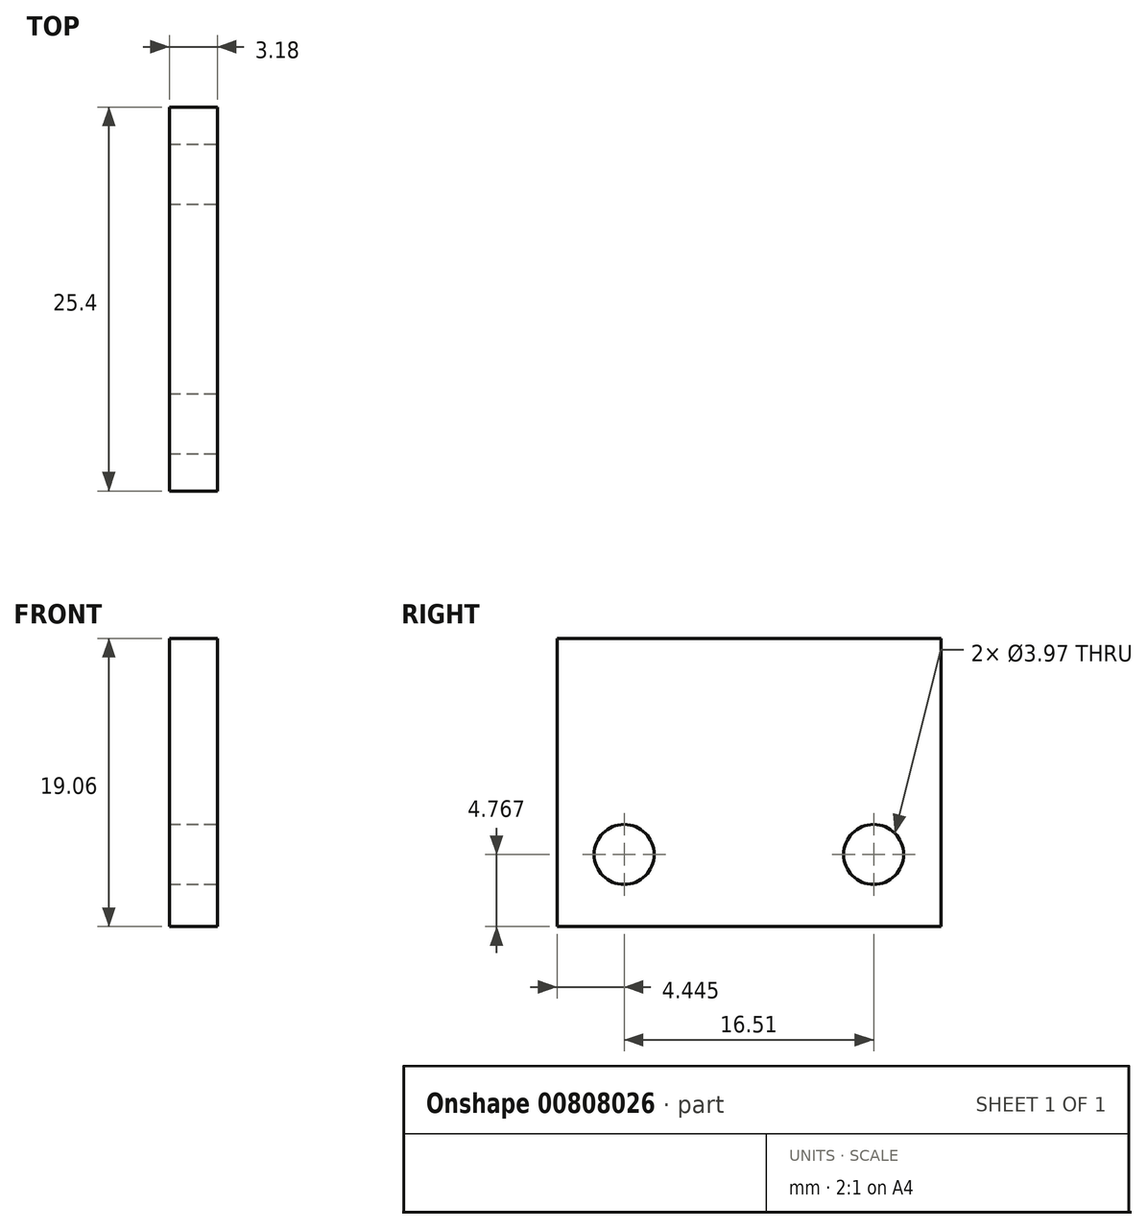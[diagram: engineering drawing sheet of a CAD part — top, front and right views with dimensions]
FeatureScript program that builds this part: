
annotation { "Feature Type Name" : "Feature", "Feature Type Description" : "" }
export const myFeature = defineFeature(function(context is Context, id is Id, definition is map)
    precondition{}
    {
        {
            var Q0;
            Q0=qCreatedBy(makeId("Right.planeOp"),FACE);
            var sketch = newSketch(context, id + "F0", { "sketchPlane" : qUnion([Q0])});
            skLineSegment(sketch, "E0.bottom", {"start": v(12.7, -9.53) * mm, "end": v(-12.7, -9.53) * mm});
            skLineSegment(sketch, "E0.top", {"start": v(12.7, 9.53) * mm, "end": v(-12.7, 9.52) * mm});
            skLineSegment(sketch, "E0.left", {"start": v(12.7, -9.52) * mm, "end": v(12.7, 9.53) * mm});
            skLineSegment(sketch, "E0.right", {"start": v(-12.7, -9.53) * mm, "end": v(-12.7, 9.52) * mm});
            skPoint(sketch, "E0.middle", {"position": v(0, 0) * mm});
            skSolve(sketch);
        }
        {
            var Q0;
            Q0 = qSketchRegion(id + "F0", true);
            extrude(context, id + "F1", {"entities" : qUnion([Q0]), "oppositeDirection" : true, "depth" : 3.17 * mm, "offsetDistance" : 25.4 * mm});
        }
        {
            var Q0;
            Q0=makeQuery(id+"F1.opExtrude","CAP_FACE",FACE,{"disambiguationData":[OSD([sQuery(id+"F0.wireOp",EDGE,"E0.bottom"),sQuery(id+"F0.wireOp",EDGE,"E0.top"),sQuery(id+"F0.wireOp",EDGE,"E0.left"),sQuery(id+"F0.wireOp",EDGE,"E0.right")])],"isStart":true});
            var sketch = newSketch(context, id + "F2", { "sketchPlane" : qUnion([Q0])});
            skLineSegment(sketch, "E1", {"start": v(-12.7, 0) * mm, "end": v(-12.7, -9.53) * mm});
            skLineSegment(sketch, "E2", {"start": v(-12.7, -4.76) * mm, "end": v(12.7, -4.76) * mm});
            skCircle(sketch, "E3", {"center": v(-8.25, -4.76) * mm, "radius": 1.98 * mm});
            skCircle(sketch, "E4", {"center": v(8.26, -4.76) * mm, "radius": 1.98 * mm});
            skSolve(sketch);
        }
        {
            var Q0;
            Q0 = qSketchRegion(id + "F2", true);
            extrude(context, id + "F3", {"entities" : qUnion([Q0]), "operationType" : NewBodyOperationType.REMOVE, "endBound" : BoundingType.THROUGH_ALL, "oppositeDirection" : true, "depth" : 25.4 * mm, "offsetDistance" : 25.4 * mm});
        }
    });
